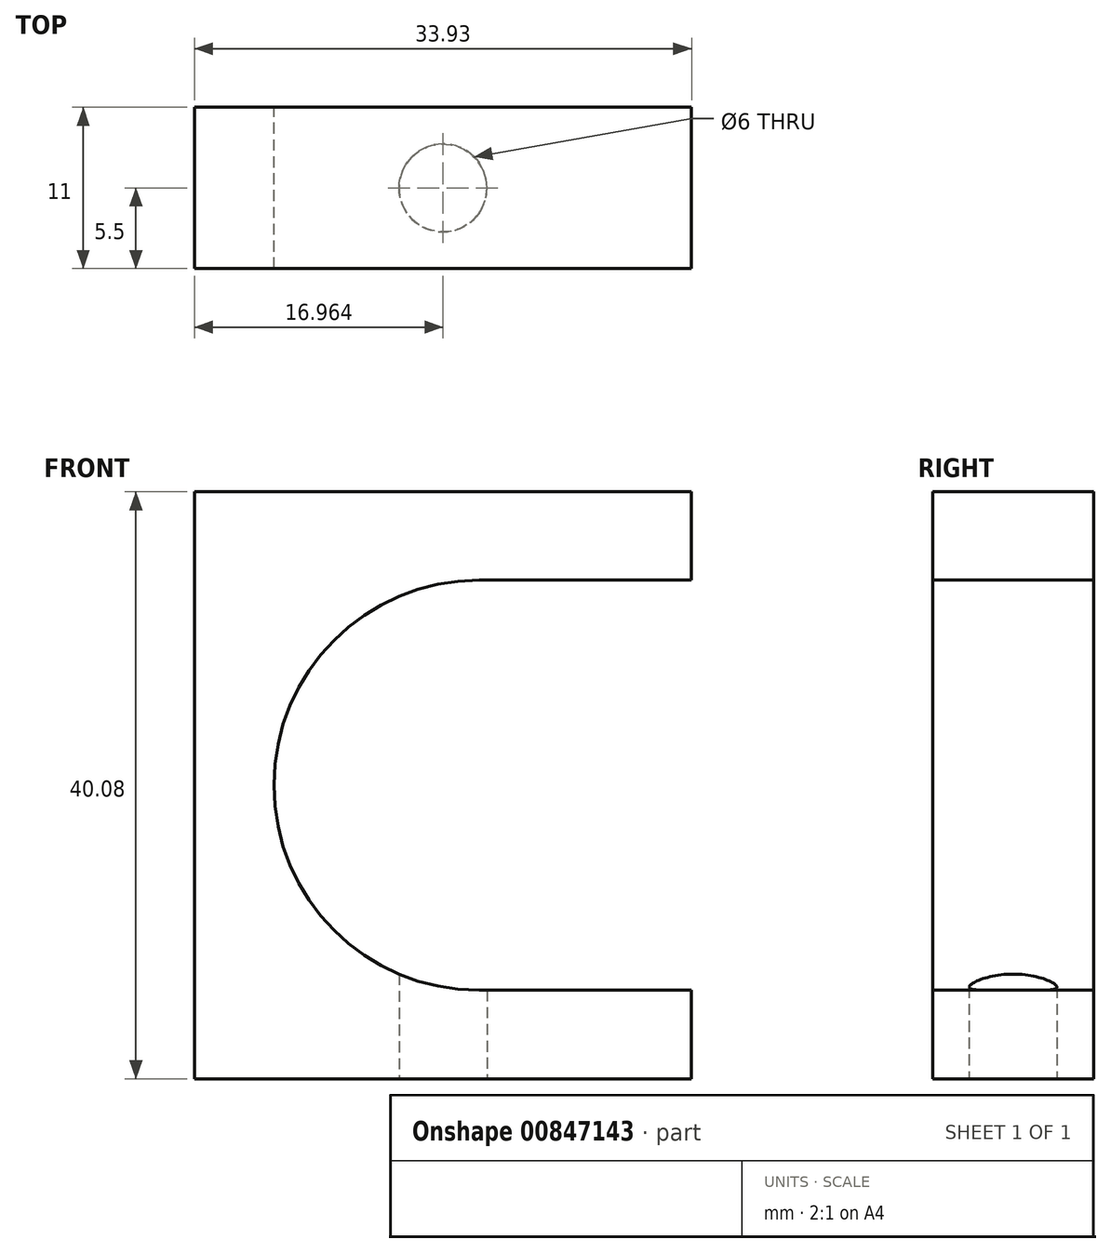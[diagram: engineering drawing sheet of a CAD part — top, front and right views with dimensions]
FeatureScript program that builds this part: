
annotation { "Feature Type Name" : "Feature", "Feature Type Description" : "" }
export const myFeature = defineFeature(function(context is Context, id is Id, definition is map)
    precondition{}
    {
        {
            assignVariable(context, id + "F0", {"name" : "width", "anyValue" : 11});
        }
        {
            var Q0;
            Q0=qCreatedBy(makeId("Front.planeOp"),FACE);
            var sketch = newSketch(context, id + "F1", { "sketchPlane" : qUnion([Q0])});
            skLineSegment(sketch, "E0.bottom", {"start": v(19.42, 20.04) * mm, "end": v(-19.42, 20.04) * mm});
            skLineSegment(sketch, "E0.top", {"start": v(19.42, -20.04) * mm, "end": v(-19.42, -20.04) * mm});
            skLineSegment(sketch, "E0.left", {"start": v(19.42, 20.04) * mm, "end": v(19.42, -20.04) * mm});
            skLineSegment(sketch, "E0.right", {"start": v(-19.42, 20.04) * mm, "end": v(-19.42, -20.04) * mm});
            skPoint(sketch, "E0.middle", {"position": v(0, 0) * mm});
            skCircle(sketch, "E1", {"center": v(0, 0) * mm, "radius": 14 * mm});
            skLineSegment(sketch, "E2", {"start": v(0, 14) * mm, "end": v(19.42, 14) * mm});
            skLineSegment(sketch, "E3", {"start": v(0, -14) * mm, "end": v(19.42, -14) * mm});
            skLineSegment(sketch, "E4", {"start": v(14.5, 20.04) * mm, "end": v(14.5, -20.04) * mm});
            skSolve(sketch);
        }
        {
            var Q0;
            {var subQ0=sQuery(id+"F1.wireOp",EDGE,"E0.right");Q0=makeQuery(id+"F1.imprint","IMPRINT",FACE,{"disambiguationData":[TD([[makeQuery(id+"F1.imprint","IMPRINT",EDGE,{"derivedFrom":subQ0}),1.0]])]});}
            extrude(context, id + "F2", {"entities" : qUnion([Q0]), "depth" : (getVariable(context, 'width')) * mm, "offsetDistance" : 25 * mm});
        }
        {
            var Q0;
            Q0=makeQuery(id+"F2.opExtrude","SWEPT_FACE",FACE,{"disambiguationData":[OSD([sQuery(id+"F1.wireOp",EDGE,"E0.top")])]});
            var sketch = newSketch(context, id + "F3", { "sketchPlane" : qUnion([Q0])});
            skLineSegment(sketch, "E5", {"start": v(-2.46, 0) * mm, "end": v(-2.46, 11) * mm});
            skCircle(sketch, "E6", {"center": v(-2.46, 5.5) * mm, "radius": 3 * mm});
            skSolve(sketch);
        }
        {
            var Q0;
            {var subQ0=sQuery(id+"F3.wireOp",EDGE,"E6");var subQ1=sQuery(id+"F3.wireOp",EDGE,"E5");var subQ2=makeQuery(id+"F3.imprint","INTERSECT",VERTEX,{"disambiguationData":[OD(0.0)],"derivedFrom":[subQ1,subQ0]});Q0=makeQuery(id+"F3.imprint","IMPRINT",FACE,{"disambiguationData":[TD([[makeQuery(id+"F3.imprint","IMPRINT",EDGE,{"disambiguationData":[TD([[subQ2,-1.0]])],"derivedFrom":subQ1}),-1.0]])]});}
            var Q1;
            {var subQ0=sQuery(id+"F3.wireOp",EDGE,"E6");var subQ1=sQuery(id+"F3.wireOp",EDGE,"E5");var subQ2=makeQuery(id+"F3.imprint","INTERSECT",VERTEX,{"disambiguationData":[OD(0.0)],"derivedFrom":[subQ1,subQ0]});Q1=makeQuery(id+"F3.imprint","IMPRINT",FACE,{"disambiguationData":[TD([[makeQuery(id+"F3.imprint","IMPRINT",EDGE,{"disambiguationData":[TD([[subQ2,-1.0]])],"derivedFrom":subQ1}),1.0]])]});}
            extrude(context, id + "F4", {"entities" : qUnion([Q0, Q1]), "operationType" : NewBodyOperationType.REMOVE, "endBound" : BoundingType.UP_TO_NEXT, "oppositeDirection" : true, "depth" : 25 * mm, "offsetDistance" : 25 * mm});
        }
    });
